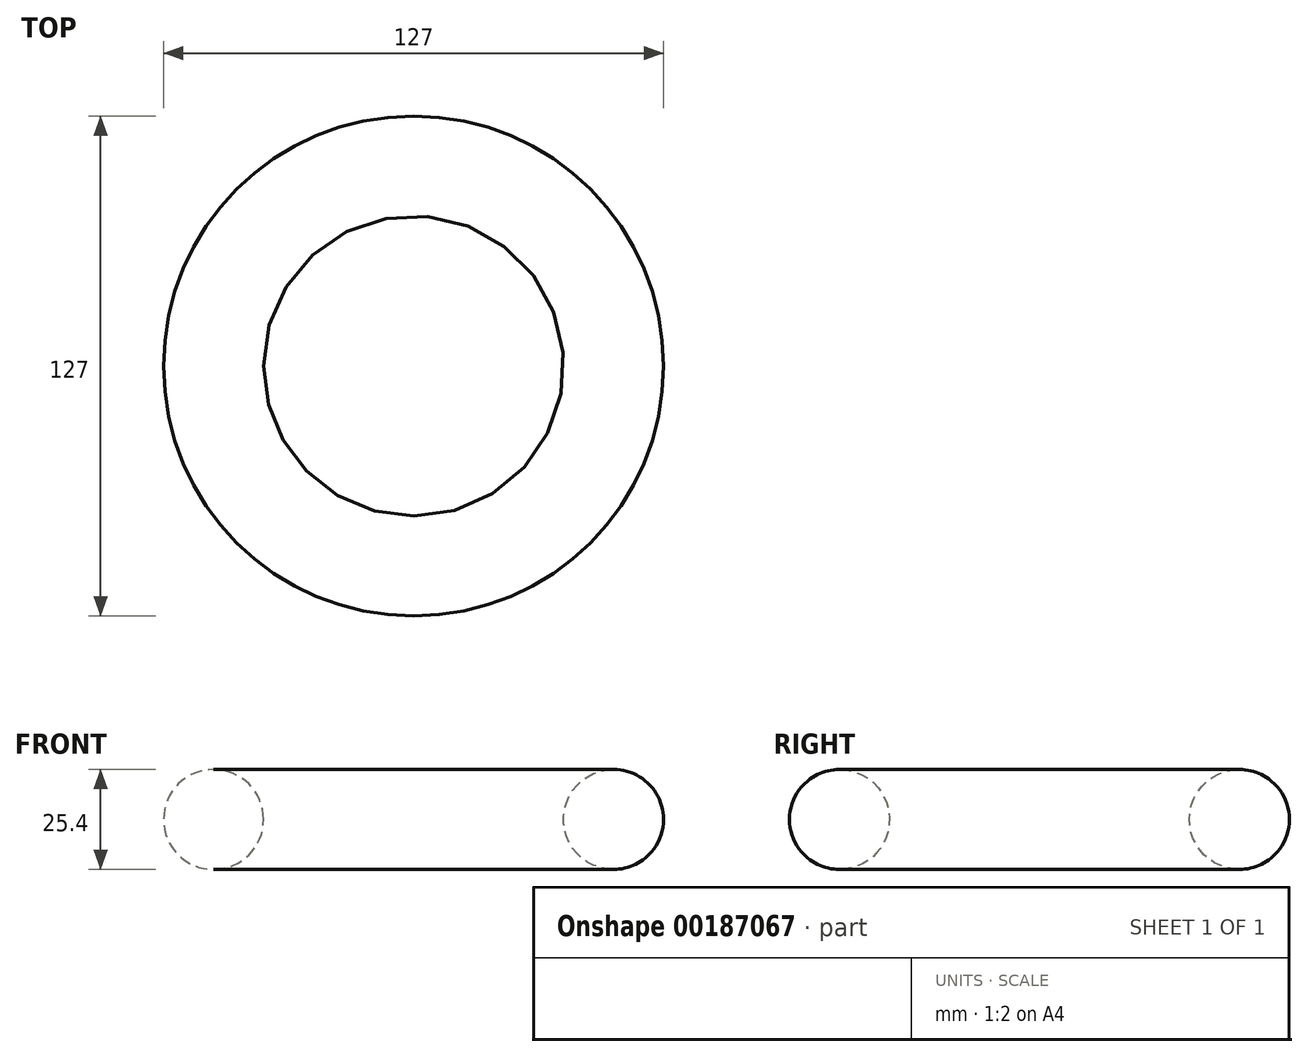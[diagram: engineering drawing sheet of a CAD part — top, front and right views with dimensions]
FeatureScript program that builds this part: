
annotation { "Feature Type Name" : "Feature", "Feature Type Description" : "" }
export const myFeature = defineFeature(function(context is Context, id is Id, definition is map)
    precondition{}
    {
        {
            var Q0;
            Q0=qCreatedBy(makeId("Front.planeOp"),FACE);
            var sketch = newSketch(context, id + "F0", { "sketchPlane" : qUnion([Q0])});
            skCircle(sketch, "E0", {"center": v(50.8, 0) * mm, "radius": 12.7 * mm});
            skLineSegment(sketch, "E1", {"start": v(0, 0) * mm, "end": v(0, 29.23) * mm});
            skSolve(sketch);
        }
        {
            var Q0;
            Q0=makeQuery(id+"F0.imprint","IMPRINT",FACE,{"disambiguationData":[TD([[makeQuery(id+"F0.imprint","IMPRINT",EDGE,{"derivedFrom":sQuery(id+"F0.wireOp",EDGE,"E0")}),1.0]])]});
            var Q1;
            Q1=sQuery(id+"F0.wireOp",EDGE,"E1");
            revolve(context, id + "F1", {"entities" : qUnion([Q0]), "axis" : qUnion([Q1]), "revolveType" : RevolveType.FULL});
        }
    });
